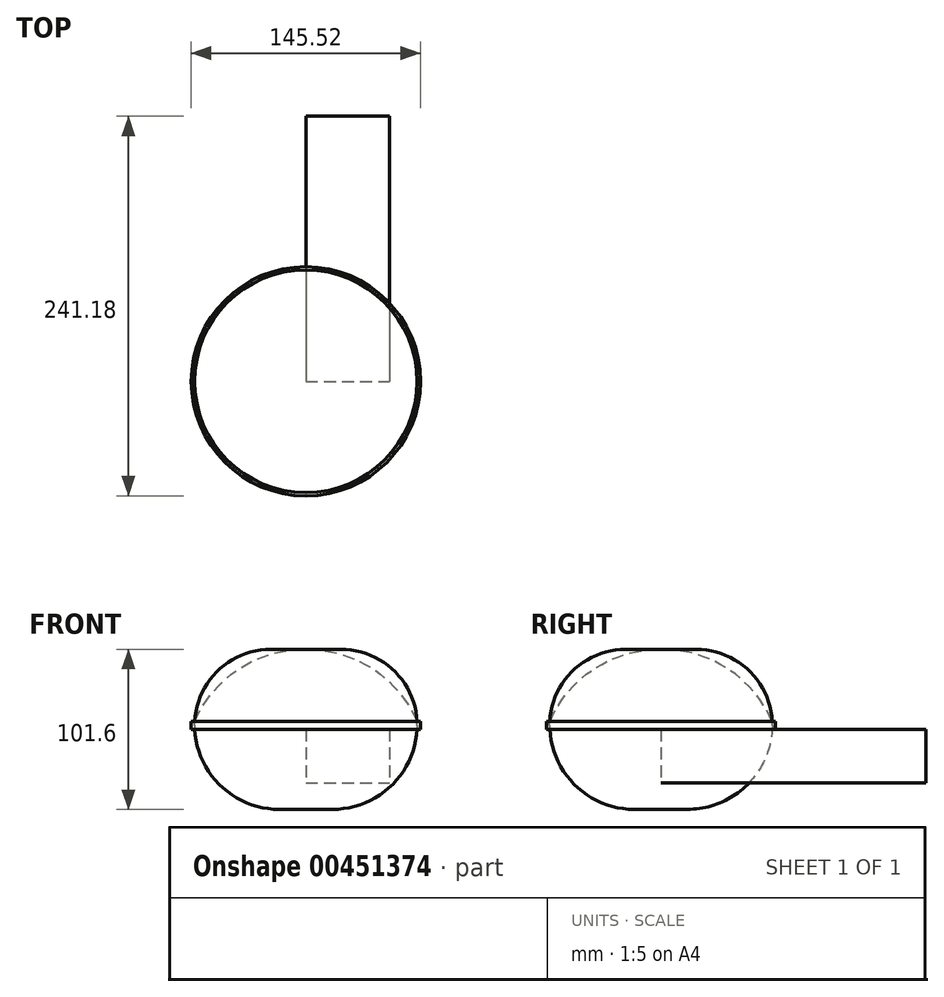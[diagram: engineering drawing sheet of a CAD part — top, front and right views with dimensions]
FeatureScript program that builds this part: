
annotation { "Feature Type Name" : "Feature", "Feature Type Description" : "" }
export const myFeature = defineFeature(function(context is Context, id is Id, definition is map)
    precondition{}
    {
        {
            var Q0;
            Q0=qCreatedBy(makeId("Top.planeOp"),FACE);
            var sketch = newSketch(context, id + "F0", { "sketchPlane" : qUnion([Q0])});
            skLineSegment(sketch, "E0.bottom", {"start": v(14.71, 66.8) * mm, "end": v(84.51, 66.8) * mm});
            skLineSegment(sketch, "E0.top", {"start": v(14.71, -56) * mm, "end": v(84.51, -56) * mm});
            skLineSegment(sketch, "E0.left", {"start": v(14.71, 66.8) * mm, "end": v(14.71, -56) * mm});
            skLineSegment(sketch, "E0.right", {"start": v(84.51, 66.8) * mm, "end": v(84.51, -56) * mm});
            skSolve(sketch);
        }
        {
            var Q0;
            Q0=makeQuery(id+"F0.imprint","IMPRINT",FACE,{"disambiguationData":[TD([[makeQuery(id+"F0.imprint","IMPRINT",EDGE,{"derivedFrom":sQuery(id+"F0.wireOp",EDGE,"E0.bottom")}),-1.0]])]});
            extrude(context, id + "F1", {"entities" : qUnion([Q0]), "depth" : 55.88 * mm});
        }
        {
            var Q0;
            Q0=makeQuery(id+"F1.opExtrude","SWEPT_BODY",BODY,{"disambiguationData":[OSD([sQuery(id+"F0.wireOp",EDGE,"E0.bottom"),sQuery(id+"F0.wireOp",EDGE,"E0.top"),sQuery(id+"F0.wireOp",EDGE,"E0.left"),sQuery(id+"F0.wireOp",EDGE,"E0.right")])]});
            deleteBodies(context, id + "F2", {"entities" : qUnion([Q0])});
        }
        {
            var Q0;
            Q0=qCreatedBy(makeId("Top.planeOp"),FACE);
            var sketch = newSketch(context, id + "F3", { "sketchPlane" : qUnion([Q0])});
            skLineSegment(sketch, "E1.bottom", {"start": v(10.73, 78) * mm, "end": v(63.93, 78) * mm});
            skLineSegment(sketch, "E1.top", {"start": v(10.73, -90.42) * mm, "end": v(63.93, -90.42) * mm});
            skLineSegment(sketch, "E1.left", {"start": v(10.73, 78) * mm, "end": v(10.73, -90.42) * mm});
            skLineSegment(sketch, "E1.right", {"start": v(63.93, 78) * mm, "end": v(63.93, -90.42) * mm});
            skSolve(sketch);
        }
        {
            var Q0;
            Q0=makeQuery(id+"F3.imprint","IMPRINT",FACE,{"disambiguationData":[TD([[makeQuery(id+"F3.imprint","IMPRINT",EDGE,{"derivedFrom":sQuery(id+"F3.wireOp",EDGE,"E1.bottom")}),-1.0]])]});
            extrude(context, id + "F4", {"entities" : qUnion([Q0]), "depth" : 33.87 * mm});
        }
        {
            var Q0;
            Q0=makeQuery(id+"F4.opExtrude","CAP_FACE",FACE,{"disambiguationData":[OSD([sQuery(id+"F3.wireOp",EDGE,"E1.bottom"),sQuery(id+"F3.wireOp",EDGE,"E1.top"),sQuery(id+"F3.wireOp",EDGE,"E1.left"),sQuery(id+"F3.wireOp",EDGE,"E1.right")])],"isStart":false});
            var sketch = newSketch(context, id + "F5", { "sketchPlane" : qUnion([Q0])});
            skCircle(sketch, "E2", {"center": v(10.73, -90.42) * mm, "radius": 72.76 * mm});
            skSolve(sketch);
        }
        {
            var Q0;
            {var subQ5=makeQuery(id+"F4.opExtrude","CAP_EDGE",EDGE,{"disambiguationData":[OSD([sQuery(id+"F3.wireOp",EDGE,"E1.top")])],"isStart":false});Q0=makeQuery(id+"F5.imprint","IMPRINT",FACE,{"disambiguationData":[TD([[makeQuery(id+"F5.imprint","IMPRINT",EDGE,{"derivedFrom":subQ5}),-1.0]])]});}
            var Q1;
            {var subQ5=makeQuery(id+"F4.opExtrude","CAP_EDGE",EDGE,{"disambiguationData":[OSD([sQuery(id+"F3.wireOp",EDGE,"E1.top")])],"isStart":false});Q1=makeQuery(id+"F5.imprint","IMPRINT",FACE,{"disambiguationData":[TD([[makeQuery(id+"F5.imprint","IMPRINT",EDGE,{"derivedFrom":subQ5}),1.0]])]});}
            extrude(context, id + "F6", {"entities" : qUnion([Q0, Q1]), "operationType" : NewBodyOperationType.ADD, "depth" : 5.02 * mm});
        }
        {
            var Q0;
            Q0=makeQuery(id+"F4.opExtrude","CAP_FACE",FACE,{"disambiguationData":[OSD([sQuery(id+"F3.wireOp",EDGE,"E1.bottom"),sQuery(id+"F3.wireOp",EDGE,"E1.top"),sQuery(id+"F3.wireOp",EDGE,"E1.left"),sQuery(id+"F3.wireOp",EDGE,"E1.right")])],"isStart":false});
            var sketch = newSketch(context, id + "F7", { "sketchPlane" : qUnion([Q0])});
            skCircle(sketch, "E3", {"center": v(10.73, -90.42) * mm, "radius": 70.7 * mm});
            skSolve(sketch);
        }
        {
            var Q0;
            Q0=makeQuery(id+"F7.imprint","IMPRINT",FACE,{"disambiguationData":[TD([[makeQuery(id+"F7.imprint","IMPRINT",EDGE,{"derivedFrom":sQuery(id+"F7.wireOp",EDGE,"E3")}),1.0]])]});
            var Q1;
            Q1=sQuery(id+"F7.wireOp",EDGE,"E3");
            extrude(context, id + "F8", {"entities" : qUnion([Q0]), "operationType" : NewBodyOperationType.ADD, "surfaceEntities" : qUnion([Q1]), "depth" : 50.8 * mm});
        }
        {
            var Q0;
            Q0=makeQuery(id+"F8.opExtrude","CAP_FACE",FACE,{"disambiguationData":[OSD([sQuery(id+"F7.wireOp",EDGE,"E3")])],"isStart":false});
            extrude(context, id + "F9", {"entities" : qUnion([Q0]), "oppositeDirection" : true, "depth" : 101.6 * mm});
        }
        {
            var Q0;
            Q0=makeQuery(id+"F8.opExtrude","CAP_EDGE",EDGE,{"disambiguationData":[OSD([sQuery(id+"F7.wireOp",EDGE,"E3")])],"isStart":false});
            fillet(context, id + "F10", {"entities" : qUnion([Q0]), "radius" : 76.2 * mm, "tangentPropagation" : true, "allowEdgeOverflow" : false});
        }
        {
            var Q0;
            Q0=makeQuery(id+"F9.opExtrude","CAP_EDGE",EDGE,{"disambiguationData":[OSD([sQuery(id+"F7.wireOp",EDGE,"E3")])],"isStart":true});
            var Q1;
            Q1=makeQuery(id+"F9.opExtrude","CAP_FACE",FACE,{"disambiguationData":[OSD([sQuery(id+"F7.wireOp",EDGE,"E3")])],"isStart":true});
            fillet(context, id + "F11", {"entities" : qUnion([Q0, Q1]), "radius" : 48.23 * mm, "tangentPropagation" : true, "allowEdgeOverflow" : false});
        }
        {
            var Q0;
            Q0=makeQuery(id+"F9.opExtrude","CAP_EDGE",EDGE,{"disambiguationData":[OSD([sQuery(id+"F7.wireOp",EDGE,"E3")])],"isStart":false});
            fillet(context, id + "F12", {"entities" : qUnion([Q0]), "radius" : 53.7 * mm, "tangentPropagation" : true, "allowEdgeOverflow" : false});
        }
    });
